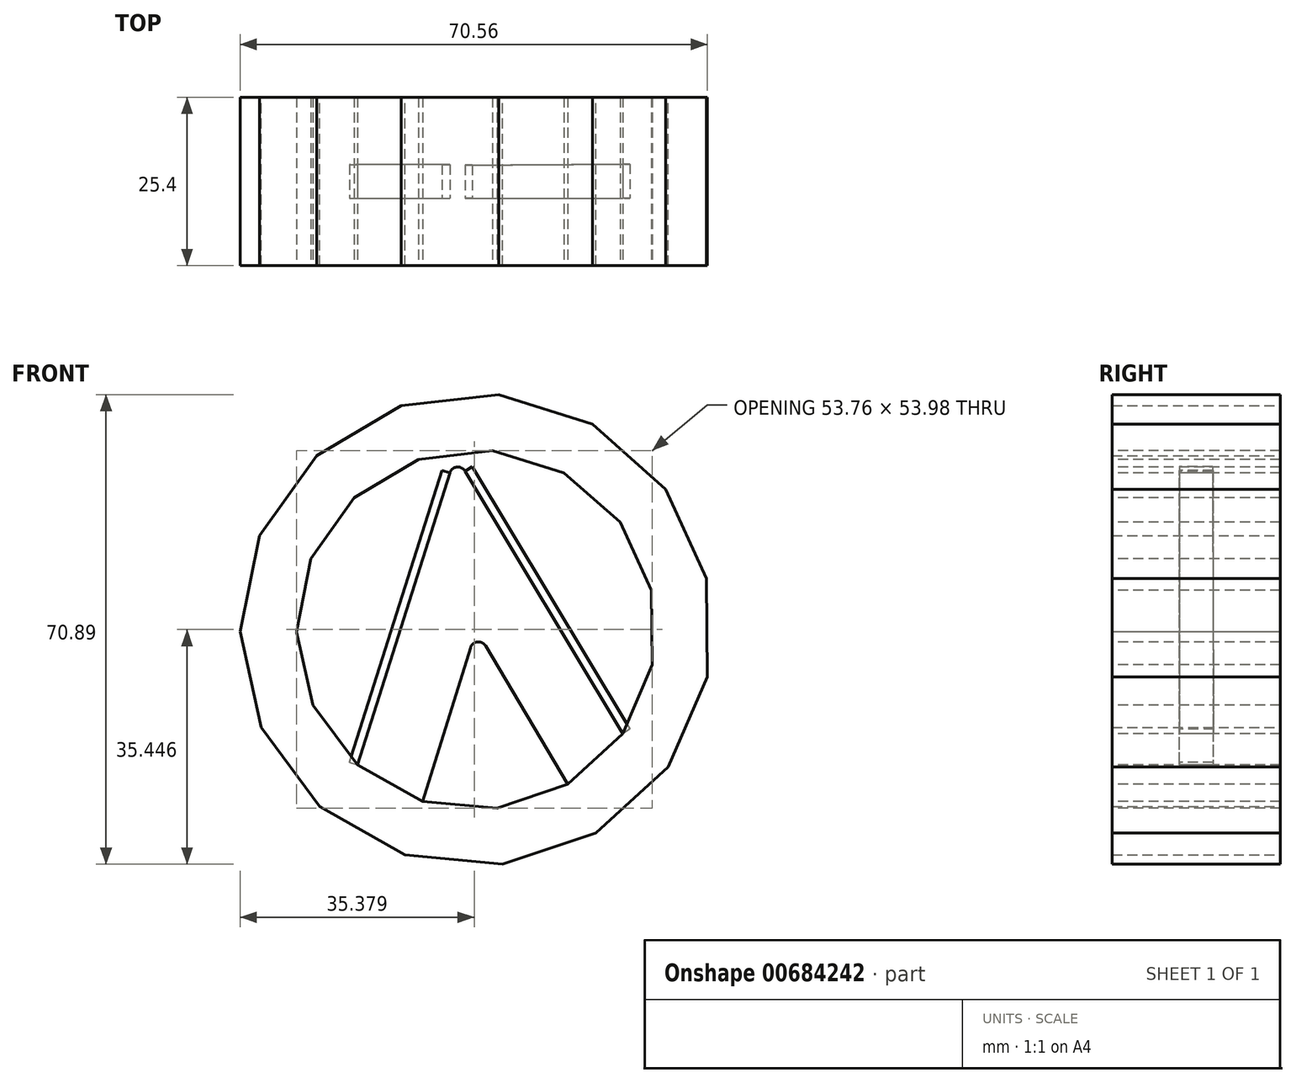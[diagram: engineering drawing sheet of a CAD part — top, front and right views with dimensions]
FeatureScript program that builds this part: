
annotation { "Feature Type Name" : "Feature", "Feature Type Description" : "" }
export const myFeature = defineFeature(function(context is Context, id is Id, definition is map)
    precondition{}
    {
        {
            var Q0;
            Q0=qCreatedBy(makeId("Front.planeOp"),FACE);
            var sketch = newSketch(context, id + "F0", { "sketchPlane" : qUnion([Q0])});
            skCircle(sketch, "E0.cCircle", {"center": v(0, 0) * mm, "radius": 34.86 * mm, "construction": true});
            skLineSegment(sketch, "E0.0", {"start": v(-24.07, 26.29) * mm, "end": v(-11.3, 33.8) * mm});
            skLineSegment(sketch, "E0.1", {"start": v(-11.3, 33.8) * mm, "end": v(3.43, 35.48) * mm});
            skLineSegment(sketch, "E0.2", {"start": v(3.43, 35.48) * mm, "end": v(17.56, 31.01) * mm});
            skLineSegment(sketch, "E0.3", {"start": v(17.56, 31.01) * mm, "end": v(28.66, 21.19) * mm});
            skLineSegment(sketch, "E0.4", {"start": v(28.66, 21.19) * mm, "end": v(34.8, 7.7) * mm});
            skLineSegment(sketch, "E0.5", {"start": v(34.8, 7.7) * mm, "end": v(34.92, -7.12) * mm});
            skLineSegment(sketch, "E0.6", {"start": v(34.92, -7.12) * mm, "end": v(29, -20.7) * mm});
            skLineSegment(sketch, "E0.7", {"start": v(29, -20.7) * mm, "end": v(18.08, -30.72) * mm});
            skLineSegment(sketch, "E0.8", {"start": v(18.08, -30.72) * mm, "end": v(4.02, -35.41) * mm});
            skLineSegment(sketch, "E0.9", {"start": v(4.02, -35.41) * mm, "end": v(-10.73, -33.99) * mm});
            skLineSegment(sketch, "E0.10", {"start": v(-10.73, -33.99) * mm, "end": v(-23.63, -26.68) * mm});
            skLineSegment(sketch, "E0.11", {"start": v(-23.63, -26.68) * mm, "end": v(-32.44, -14.77) * mm});
            skLineSegment(sketch, "E0.12", {"start": v(-32.44, -14.77) * mm, "end": v(-35.64, -0.3) * mm});
            skLineSegment(sketch, "E0.13", {"start": v(-35.64, -0.3) * mm, "end": v(-32.68, 14.23) * mm});
            skLineSegment(sketch, "E0.14", {"start": v(-32.68, 14.23) * mm, "end": v(-24.07, 26.29) * mm});
            skPoint(sketch, "E0.0.midPoint", {"position": v(-17.68, 30.05) * mm});
            skSolve(sketch);
        }
        {
            var Q0;
            Q0=makeQuery(id+"F0.imprint","IMPRINT",FACE,{"disambiguationData":[TD([[makeQuery(id+"F0.imprint","IMPRINT",EDGE,{"derivedFrom":sQuery(id+"F0.wireOp",EDGE,"E0.0")}),-1.0]])]});
            extrude(context, id + "F1", {"entities" : qUnion([Q0]), "depth" : 25.4 * mm, "offsetDistance" : 25.4 * mm});
        }
        {
            var Q0;
            Q0=makeQuery(id+"F1.opExtrude","CAP_FACE",FACE,{"disambiguationData":[OSD([sQuery(id+"F0.wireOp",EDGE,"E0.0"),sQuery(id+"F0.wireOp",EDGE,"E0.1"),sQuery(id+"F0.wireOp",EDGE,"E0.2"),sQuery(id+"F0.wireOp",EDGE,"E0.3"),sQuery(id+"F0.wireOp",EDGE,"E0.4"),sQuery(id+"F0.wireOp",EDGE,"E0.5"),sQuery(id+"F0.wireOp",EDGE,"E0.6"),sQuery(id+"F0.wireOp",EDGE,"E0.7"),sQuery(id+"F0.wireOp",EDGE,"E0.8"),sQuery(id+"F0.wireOp",EDGE,"E0.9"),sQuery(id+"F0.wireOp",EDGE,"E0.10"),sQuery(id+"F0.wireOp",EDGE,"E0.11"),sQuery(id+"F0.wireOp",EDGE,"E0.12"),sQuery(id+"F0.wireOp",EDGE,"E0.13"),sQuery(id+"F0.wireOp",EDGE,"E0.14")])],"isStart":false});
            var sketch = newSketch(context, id + "F2", { "sketchPlane" : qUnion([Q0])});
            skCircle(sketch, "E1.cCircle", {"center": v(0, 0) * mm, "radius": 27.14 * mm, "construction": true});
            skLineSegment(sketch, "E1.0", {"start": v(-8.71, 25.7) * mm, "end": v(2.5, 27.03) * mm});
            skLineSegment(sketch, "E1.1", {"start": v(2.5, 27.03) * mm, "end": v(13.27, 23.68) * mm});
            skLineSegment(sketch, "E1.2", {"start": v(13.27, 23.68) * mm, "end": v(21.75, 16.23) * mm});
            skLineSegment(sketch, "E1.3", {"start": v(21.75, 16.23) * mm, "end": v(26.47, 5.98) * mm});
            skLineSegment(sketch, "E1.4", {"start": v(26.47, 5.98) * mm, "end": v(26.62, -5.3) * mm});
            skLineSegment(sketch, "E1.5", {"start": v(26.62, -5.3) * mm, "end": v(22.16, -15.67) * mm});
            skLineSegment(sketch, "E1.6", {"start": v(22.16, -15.67) * mm, "end": v(13.87, -23.33) * mm});
            skLineSegment(sketch, "E1.7", {"start": v(13.87, -23.33) * mm, "end": v(3.18, -26.95) * mm});
            skLineSegment(sketch, "E1.8", {"start": v(3.18, -26.95) * mm, "end": v(-8.06, -25.92) * mm});
            skLineSegment(sketch, "E1.9", {"start": v(-8.06, -25.92) * mm, "end": v(-17.9, -20.4) * mm});
            skLineSegment(sketch, "E1.10", {"start": v(-17.9, -20.4) * mm, "end": v(-24.65, -11.35) * mm});
            skLineSegment(sketch, "E1.11", {"start": v(-24.65, -11.35) * mm, "end": v(-27.14, -0.34) * mm});
            skLineSegment(sketch, "E1.12", {"start": v(-27.14, -0.34) * mm, "end": v(-24.93, 10.72) * mm});
            skLineSegment(sketch, "E1.13", {"start": v(-24.93, 10.72) * mm, "end": v(-18.42, 19.94) * mm});
            skLineSegment(sketch, "E1.14", {"start": v(-18.42, 19.94) * mm, "end": v(-8.71, 25.7) * mm});
            skSolve(sketch);
        }
        {
            var Q0;
            Q0=makeQuery(id+"F2.imprint","IMPRINT",FACE,{"disambiguationData":[TD([[makeQuery(id+"F2.imprint","IMPRINT",EDGE,{"derivedFrom":sQuery(id+"F2.wireOp",EDGE,"E1.0")}),-1.0]])]});
            extrude(context, id + "F3", {"entities" : qUnion([Q0]), "operationType" : NewBodyOperationType.REMOVE, "oppositeDirection" : true, "depth" : 25.4 * mm, "offsetDistance" : 25.4 * mm});
        }
        {
            var Q0;
            Q0=makeQuery(id+"F1.opExtrude","CAP_FACE",FACE,{"disambiguationData":[OSD([sQuery(id+"F0.wireOp",EDGE,"E0.0"),sQuery(id+"F0.wireOp",EDGE,"E0.1"),sQuery(id+"F0.wireOp",EDGE,"E0.2"),sQuery(id+"F0.wireOp",EDGE,"E0.3"),sQuery(id+"F0.wireOp",EDGE,"E0.4"),sQuery(id+"F0.wireOp",EDGE,"E0.5"),sQuery(id+"F0.wireOp",EDGE,"E0.6"),sQuery(id+"F0.wireOp",EDGE,"E0.7"),sQuery(id+"F0.wireOp",EDGE,"E0.8"),sQuery(id+"F0.wireOp",EDGE,"E0.9"),sQuery(id+"F0.wireOp",EDGE,"E0.10"),sQuery(id+"F0.wireOp",EDGE,"E0.11"),sQuery(id+"F0.wireOp",EDGE,"E0.12"),sQuery(id+"F0.wireOp",EDGE,"E0.13"),sQuery(id+"F0.wireOp",EDGE,"E0.14")])],"isStart":false});
            var sketch = newSketch(context, id + "F4", { "sketchPlane" : qUnion([Q0])});
            skLineSegment(sketch, "E2", {"start": v(-8.06, -25.92) * mm, "end": v(-0.85, -2.72) * mm});
            skLineSegment(sketch, "E3", {"start": v(1.46, -2.45) * mm, "end": v(13.87, -23.33) * mm});
            skLineSegment(sketch, "E4", {"start": v(13.87, -23.33) * mm, "end": v(22.16, -15.67) * mm});
            skLineSegment(sketch, "E5", {"start": v(22.16, -15.67) * mm, "end": v(-1.66, 23.95) * mm});
            skLineSegment(sketch, "E6", {"start": v(-3.96, 23.68) * mm, "end": v(-17.9, -20.4) * mm});
            skPoint(sketch, "E7.visualSharp", {"position": v(-3.1, 26.37) * mm});
            skArc(sketch, "E7.filletArc", {"start": v(-1.66, 23.95) * mm, "mid": v(-2.9, 24.56) * mm, "end": v(-3.96, 23.68) * mm});
            skPoint(sketch, "E8.visualSharp", {"position": v(0, 0) * mm});
            skArc(sketch, "E8.filletArc", {"start": v(1.46, -2.45) * mm, "mid": v(0.22, -1.84) * mm, "end": v(-0.85, -2.72) * mm});
            skSolve(sketch);
        }
        {
            var Q0;
            Q0=makeQuery(id+"F4.imprint","IMPRINT",FACE,{"disambiguationData":[TD([[makeQuery(id+"F4.imprint","IMPRINT",EDGE,{"derivedFrom":sQuery(id+"F4.wireOp",EDGE,"E2")}),1.0]])]});
            extrude(context, id + "F5", {"entities" : qUnion([Q0]), "oppositeDirection" : true, "depth" : 25.4 * mm, "offsetDistance" : 25.4 * mm});
        }
        {
            var Q0;
            Q0=makeQuery(id+"F5.opExtrude","SWEPT_FACE",FACE,{"disambiguationData":[OSD([sQuery(id+"F4.wireOp",EDGE,"E6")])]});
            var sketch = newSketch(context, id + "F6", { "sketchPlane" : qUnion([Q0])});
            skLineSegment(sketch, "E9", {"start": v(10.16, 21.38) * mm, "end": v(10.16, -24.85) * mm});
            skLineSegment(sketch, "E10", {"start": v(10.16, -24.85) * mm, "end": v(11.18, -24.87) * mm});
            skLineSegment(sketch, "E11", {"start": v(15.24, -24.85) * mm, "end": v(15.24, 21.38) * mm});
            skLineSegment(sketch, "E12", {"start": v(15.24, 21.38) * mm, "end": v(10.16, 21.38) * mm});
            skLineSegment(sketch, "E13", {"start": v(15.24, -24.85) * mm, "end": v(11.18, -24.87) * mm});
            skLineSegment(sketch, "E14", {"start": v(10.16, -24.85) * mm, "end": v(15.24, -24.85) * mm});
            skSolve(sketch);
        }
        {
            var Q0;
            Q0=makeQuery(id+"F6.imprint","IMPRINT",FACE,{"disambiguationData":[TD([[makeQuery(id+"F6.imprint","IMPRINT",EDGE,{"derivedFrom":sQuery(id+"F6.wireOp",EDGE,"E9")}),1.0]])]});
            extrude(context, id + "F7", {"entities" : qUnion([Q0]), "depth" : 1.27 * mm, "offsetDistance" : 25.4 * mm});
        }
        {
            var Q0;
            Q0=makeQuery(id+"F5.opExtrude","SWEPT_FACE",FACE,{"disambiguationData":[OSD([sQuery(id+"F4.wireOp",EDGE,"E5")])]});
            var sketch = newSketch(context, id + "F8", { "sketchPlane" : qUnion([Q0])});
            skLineSegment(sketch, "E15", {"start": v(-15.24, 21.38) * mm, "end": v(-15.24, -24.85) * mm});
            skLineSegment(sketch, "E16", {"start": v(-10.24, 21.38) * mm, "end": v(-10.08, -24.85) * mm});
            skLineSegment(sketch, "E17", {"start": v(-15.24, 21.38) * mm, "end": v(-10.24, 21.38) * mm});
            skLineSegment(sketch, "E18", {"start": v(-15.24, -24.85) * mm, "end": v(-10.08, -24.85) * mm});
            skSolve(sketch);
        }
        {
            var Q0;
            Q0=makeQuery(id+"F8.imprint","IMPRINT",FACE,{"disambiguationData":[TD([[makeQuery(id+"F8.imprint","IMPRINT",EDGE,{"derivedFrom":sQuery(id+"F8.wireOp",EDGE,"E15")}),1.0]])]});
            extrude(context, id + "F9", {"entities" : qUnion([Q0]), "depth" : 1.27 * mm, "offsetDistance" : 25.4 * mm});
        }
    });
